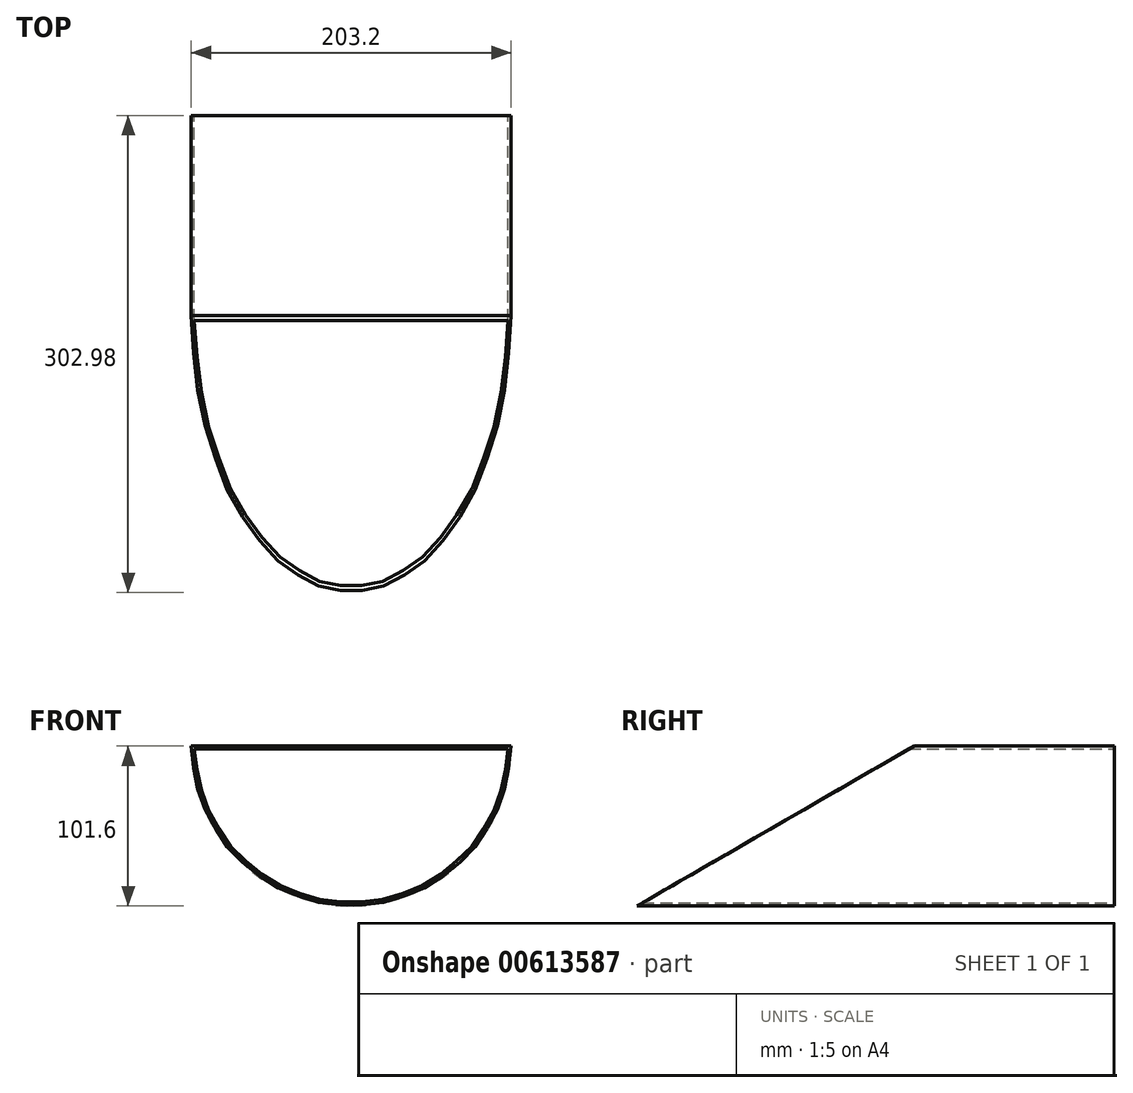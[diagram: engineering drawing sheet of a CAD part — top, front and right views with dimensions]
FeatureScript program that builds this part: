
annotation { "Feature Type Name" : "Feature", "Feature Type Description" : "" }
export const myFeature = defineFeature(function(context is Context, id is Id, definition is map)
    precondition{}
    {
        {
            var Q0;
            Q0=qCreatedBy(makeId("Front.planeOp"),FACE);
            var sketch = newSketch(context, id + "F0", { "sketchPlane" : qUnion([Q0])});
            skArc(sketch, "E0", {"start": v(-101.6, 0) * mm, "mid": v(0, -101.6) * mm, "end": v(101.6, 0) * mm});
            skLineSegment(sketch, "E1.bottom", {"start": v(-101.6, 0) * mm, "end": v(101.6, 0) * mm});
            skPoint(sketch, "E1.left.start.orphan", {"position": v(-112.71, 0) * mm});
            skLineSegment(sketch, "E2.0", {"start": v(-99.68, -1.9) * mm, "end": v(99.68, -1.9) * mm});
            skArc(sketch, "E2.1", {"start": v(-99.68, -1.9) * mm, "mid": v(0, -99.7) * mm, "end": v(99.68, -1.9) * mm});
            skSolve(sketch);
        }
        {
            var Q0;
            Q0=makeQuery(id+"F0.imprint","IMPRINT",FACE,{"disambiguationData":[TD([[makeQuery(id+"F0.imprint","IMPRINT",EDGE,{"derivedFrom":sQuery(id+"F0.wireOp",EDGE,"E0")}),1.0]])]});
            var Q1;
            Q1=makeQuery(id+"FxAh9uI6gGhRHaT_0.imprint","IMPRINT",FACE,{"disambiguationData":[TD([[makeQuery(id+"FxAh9uI6gGhRHaT_0.imprint","IMPRINT",EDGE,{"derivedFrom":sQuery(id+"FxAh9uI6gGhRHaT_0.wireOp",EDGE,"a9cdd68a-2538-4949-9c71-b066efcf1e69.0")}),-1.0]])]});
            extrude(context, id + "F1", {"entities" : qUnion([Q0, Q1]), "depth" : 304.8 * mm});
        }
        {
            var Q0;
            Q0=makeQuery(id+"F1.opExtrude","SWEPT_FACE",FACE,{"disambiguationData":[OSD([sQuery(id+"F0.wireOp",EDGE,"E1.bottom")])]});
            extrude(context, id + "F2", {"entities" : qUnion([Q0]), "depth" : 203.2 * mm});
        }
        {
            var Q0;
            Q0=makeQuery(id+"F2.opExtrude","SWEPT_BODY",BODY,{"disambiguationData":[OSD([sQuery(id+"F0.wireOp",EDGE,"E1.bottom")])]});
            var Q1;
            {var subQ0=sQuery(id+"F0.wireOp",EDGE,"E1.bottom");var subQ1=sQuery(id+"F0.wireOp",EDGE,"E0");Q1=makeQuery(id+"F2.opExtrude","CAP_EDGE",EDGE,{"disambiguationData":[OSD([subQ1,subQ0]),TDD([makeQuery(id+"F1.opExtrude","SWEPT_EDGE",EDGE,{"disambiguationData":[OSD([subQ1,subQ0]),TDD([makeQuery(id+"F0.imprint","INTERSECT",VERTEX,{"disambiguationData":[OD(1.0)],"derivedFrom":[subQ1,subQ0]})])]})])],"isStart":false});}
            transform(context, id + "F3", {"entities" : qUnion([Q0]), "transformType" : TransformType.TRANSLATION_DISTANCE, "transformDirection" : qUnion([Q1]), "distance" : 127 * mm, "oppositeDirection" : true, "makeCopy" : false});
        }
        {
            var Q0;
            Q0=makeQuery(id+"F2.opExtrude","SWEPT_BODY",BODY,{"disambiguationData":[OSD([sQuery(id+"F0.wireOp",EDGE,"E1.bottom")])]});
            var Q1;
            {var subQ0=sQuery(id+"F0.wireOp",EDGE,"E1.bottom");Q1=makeQuery(id+"F2.opExtrude","CAP_EDGE",EDGE,{"disambiguationData":[OSD([subQ0]),TDD([makeQuery(id+"F1.opExtrude","CAP_EDGE",EDGE,{"disambiguationData":[OSD([subQ0])],"isStart":true})])],"isStart":true});}
            transform(context, id + "F4", {"entities" : qUnion([Q0]), "transformType" : TransformType.ROTATION, "transformAxis" : qUnion([Q1]), "angle" : 30 * degree, "makeCopy" : false});
        }
        {
            var Q0;
            Q0=makeQuery(id+"F2.opExtrude","SWEPT_BODY",BODY,{"disambiguationData":[OSD([sQuery(id+"F0.wireOp",EDGE,"E1.bottom")])]});
            var Q1;
            Q1=makeQuery(id+"F1.opExtrude","SWEPT_BODY",BODY,{"disambiguationData":[OSD([sQuery(id+"F0.wireOp",EDGE,"E0"),sQuery(id+"F0.wireOp",EDGE,"E1.bottom")])]});
            var Q2;
            Q2=makeQuery(id+"F1.opExtrude","SWEPT_BODY",BODY,{"disambiguationData":[OSD([sQuery(id+"FxAh9uI6gGhRHaT_0.wireOp",EDGE,"a9cdd68a-2538-4949-9c71-b066efcf1e69.0"),sQuery(id+"FxAh9uI6gGhRHaT_0.wireOp",EDGE,"a9cdd68a-2538-4949-9c71-b066efcf1e69.1")])]});
            booleanBodies(context, id + "F5", {"operationType" : BooleanOperationType.SUBTRACTION, "tools" : qUnion([Q0]), "targets" : qUnion([Q1, Q2])});
        }
    });
